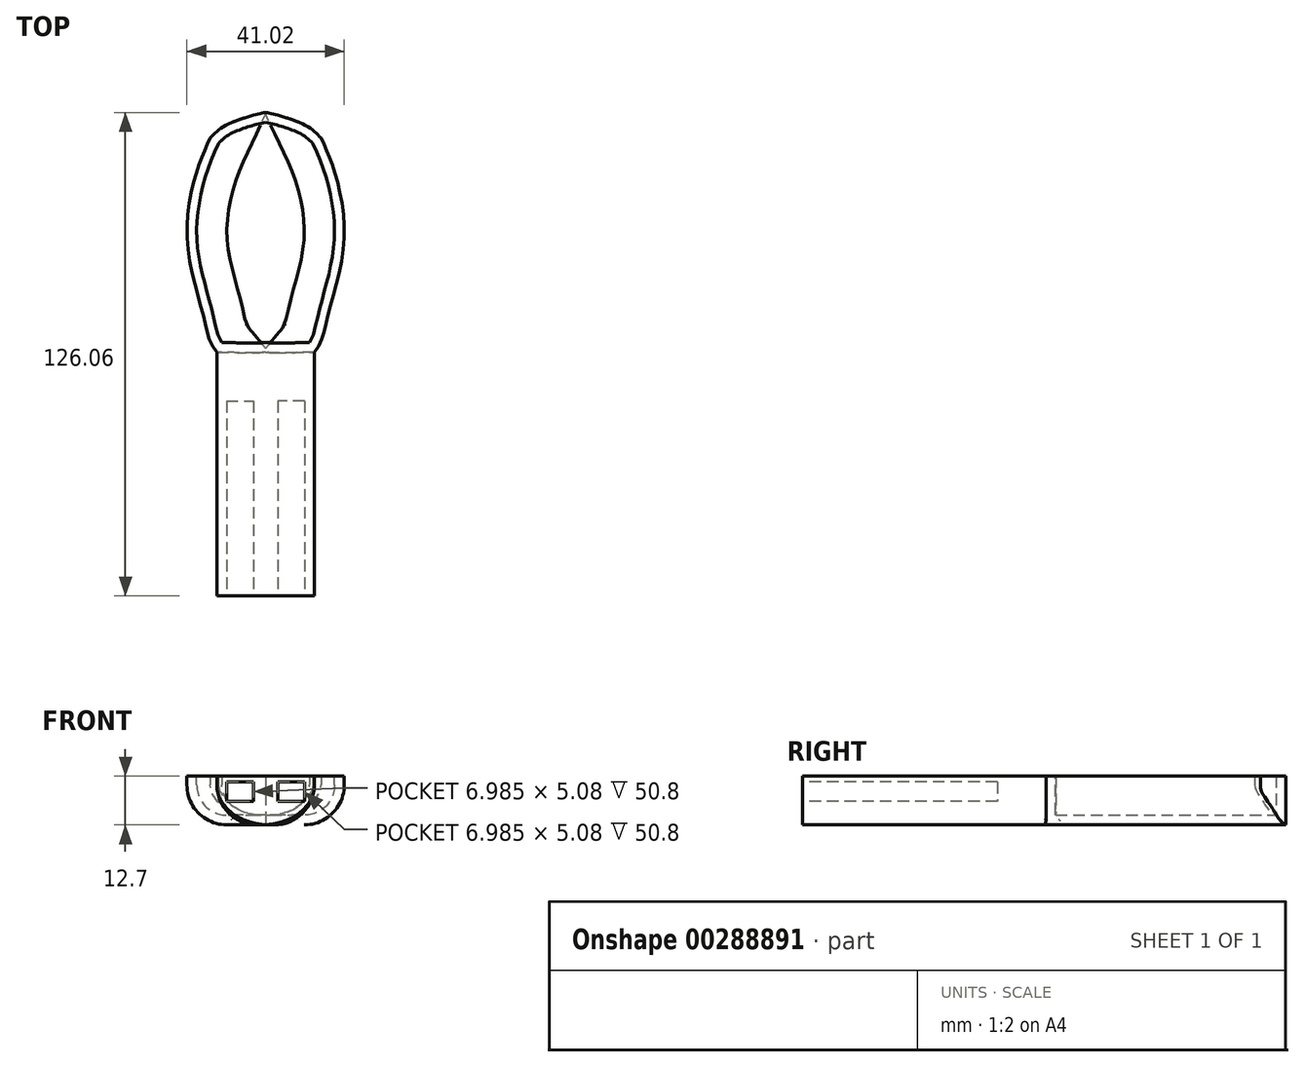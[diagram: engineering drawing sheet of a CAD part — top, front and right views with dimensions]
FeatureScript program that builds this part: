
annotation { "Feature Type Name" : "Feature", "Feature Type Description" : "" }
export const myFeature = defineFeature(function(context is Context, id is Id, definition is map)
    precondition{}
    {
        {
            var Q0;
            Q0=qCreatedBy(makeId("Top.planeOp"),FACE);
            var sketch = newSketch(context, id + "F0", { "sketchPlane" : qUnion([Q0])});
            skLineSegment(sketch, "E0", {"start": v(0, 75.51) * mm, "end": v(0, -68.28) * mm});
            skFitSpline(sketch, "E1", {"points": [v(0, -14.97) * mm, v(-12.7, -14.95) * mm], "startDerivative": vector(-9.63, -0.3) * mm, "endDerivative": vector(-10.55, 0.04) * mm});
            skFitSpline(sketch, "E2", {"points": [v(-12.7, -14.95) * mm, v(-16.24, -5.41) * mm, v(-20.45, 14.44) * mm, v(-17.75, 32.79) * mm, v(-14.44, 40.9) * mm], "startDerivative": vector(-31.58, 37.42) * mm, "endDerivative": vector(17.48, 37.1) * mm});
            skLineSegment(sketch, "E3", {"start": v(-12.7, -14.95) * mm, "end": v(-12.7, -78.45) * mm});
            skLineSegment(sketch, "E4", {"start": v(-12.7, -78.45) * mm, "end": v(0, -78.45) * mm});
            skLineSegment(sketch, "E5", {"start": v(0, -78.45) * mm, "end": v(0, -14.97) * mm});
            skFitSpline(sketch, "E6", {"points": [v(-14.44, 40.9) * mm, v(-10.85, 44) * mm, v(-3.36, 46.84) * mm, v(0, 47.61) * mm], "startDerivative": vector(9.28, 10.13) * mm, "endDerivative": vector(10.75, 2.17) * mm});
            skSolve(sketch);
        }
        {
            var Q0;
            {var subQ0=sQuery(id+"F0.wireOp",EDGE,"E1");Q0=makeQuery(id+"F0.imprint","IMPRINT",FACE,{"disambiguationData":[TD([[makeQuery(id+"F0.imprint","IMPRINT",EDGE,{"derivedFrom":subQ0}),-1.0]])]});}
            extrude(context, id + "F1", {"entities" : qUnion([Q0]), "depth" : 12.7 * mm});
        }
        {
            var Q0;
            Q0=makeQuery(id+"F1.opExtrude","CAP_EDGE",EDGE,{"disambiguationData":[OSD([sQuery(id+"F0.wireOp",EDGE,"E2")])],"isStart":true});
            var Q1;
            Q1=makeQuery(id+"F1.opExtrude","CAP_EDGE",EDGE,{"disambiguationData":[OSD([sQuery(id+"F0.wireOp",EDGE,"6Nhsaj5v-RiRn-NaKJ-OKBq-gLtByNQd9aBa")])],"isStart":true});
            var Q2;
            Q2=makeQuery(id+"F1.opExtrude","CAP_EDGE",EDGE,{"disambiguationData":[OSD([sQuery(id+"F0.wireOp",EDGE,"frloRvQW-Mg0R-VNwh-8u0Y-ItcNmjmq1O22")])],"isStart":true});
            fillet(context, id + "F2", {"entities" : qUnion([Q0, Q1, Q2]), "radius" : 10.4 * mm, "tangentPropagation" : true, "allowEdgeOverflow" : false});
        }
        {
            var Q0;
            Q0=makeQuery(id+"F1.opExtrude","SWEPT_BODY",BODY,{"disambiguationData":[OSD([sQuery(id+"F0.wireOp",EDGE,"E0"),sQuery(id+"F0.wireOp",EDGE,"E1"),sQuery(id+"F0.wireOp",EDGE,"E2"),sQuery(id+"F0.wireOp",EDGE,"6Nhsaj5v-RiRn-NaKJ-OKBq-gLtByNQd9aBa"),sQuery(id+"F0.wireOp",EDGE,"frloRvQW-Mg0R-VNwh-8u0Y-ItcNmjmq1O22")])]});
            var Q1;
            Q1=makeQuery(id+"F1.opExtrude","SWEPT_FACE",FACE,{"disambiguationData":[OSD([sQuery(id+"F0.wireOp",EDGE,"E0")])]});
            mirror(context, id + "F3", {"operationType" : NewBodyOperationType.ADD, "entities" : qUnion([Q0]), "mirrorPlane" : qUnion([Q1])});
        }
        {
            var Q0;
            {var subQ0=makeQuery(id+"F1.opExtrude","CAP_FACE",FACE,{"disambiguationData":[OSD([sQuery(id+"F0.wireOp",EDGE,"E0"),sQuery(id+"F0.wireOp",EDGE,"E1"),sQuery(id+"F0.wireOp",EDGE,"E2"),sQuery(id+"F0.wireOp",EDGE,"6Nhsaj5v-RiRn-NaKJ-OKBq-gLtByNQd9aBa"),sQuery(id+"F0.wireOp",EDGE,"frloRvQW-Mg0R-VNwh-8u0Y-ItcNmjmq1O22")])],"isStart":false});Q0=makeQuery(id+"F3.boolean.opBoolean","MERGE",FACE,{"derivedFrom":[subQ0,makeQuery(id+"F3.opPattern","COPY",FACE,{"derivedFrom":subQ0,"instanceName":"1"})]});}
            var Q1;
            Q1=makeQuery(id+"F1.opExtrude","SWEPT_BODY",BODY,{"disambiguationData":[OSD([sQuery(id+"F0.wireOp",EDGE,"E0"),sQuery(id+"F0.wireOp",EDGE,"E1"),sQuery(id+"F0.wireOp",EDGE,"E2"),sQuery(id+"F0.wireOp",EDGE,"6Nhsaj5v-RiRn-NaKJ-OKBq-gLtByNQd9aBa"),sQuery(id+"F0.wireOp",EDGE,"frloRvQW-Mg0R-VNwh-8u0Y-ItcNmjmq1O22")])]});
            shell(context, id + "F4", {"entities" : qUnion([Q0]), "parts" : qUnion([Q1]), "thickness" : 2.54 * mm});
        }
        {
            var Q0;
            {var subQ0=sQuery(id+"F0.wireOp",EDGE,"E1");Q0=makeQuery(id+"F0.imprint","IMPRINT",FACE,{"disambiguationData":[TD([[makeQuery(id+"F0.imprint","IMPRINT",EDGE,{"derivedFrom":subQ0}),1.0]])]});}
            extrude(context, id + "F5", {"entities" : qUnion([Q0]), "depth" : 12.7 * mm});
        }
        {
            var Q0;
            Q0=makeQuery(id+"F5.opExtrude","CAP_EDGE",EDGE,{"disambiguationData":[OSD([sQuery(id+"F0.wireOp",EDGE,"E3")])],"isStart":true});
            fillet(context, id + "F6", {"entities" : qUnion([Q0]), "radius" : 10.4 * mm, "tangentPropagation" : true, "allowEdgeOverflow" : false});
        }
        {
            var Q0;
            Q0=makeQuery(id+"F5.opExtrude","SWEPT_FACE",FACE,{"disambiguationData":[OSD([sQuery(id+"F0.wireOp",EDGE,"E4")])]});
            var sketch = newSketch(context, id + "F7", { "sketchPlane" : qUnion([Q0])});
            skLineSegment(sketch, "E7", {"start": v(-10.18, 11.18) * mm, "end": v(-10.18, 6.1) * mm});
            skLineSegment(sketch, "E8", {"start": v(-10.18, 11.18) * mm, "end": v(-3.2, 11.18) * mm});
            skLineSegment(sketch, "E9", {"start": v(-3.2, 11.18) * mm, "end": v(-3.2, 6.1) * mm});
            skLineSegment(sketch, "E10", {"start": v(-10.18, 6.1) * mm, "end": v(-3.2, 6.1) * mm});
            skSolve(sketch);
        }
        {
            var Q0;
            Q0=makeQuery(id+"F7.imprint","IMPRINT",FACE,{"disambiguationData":[TD([[makeQuery(id+"F7.imprint","IMPRINT",EDGE,{"derivedFrom":sQuery(id+"F7.wireOp",EDGE,"E7")}),1.0]])]});
            extrude(context, id + "F8", {"entities" : qUnion([Q0]), "operationType" : NewBodyOperationType.REMOVE, "oppositeDirection" : true, "depth" : 50.8 * mm});
        }
        {
            var Q0;
            Q0=makeQuery(id+"F5.opExtrude","SWEPT_BODY",BODY,{"disambiguationData":[OSD([sQuery(id+"F0.wireOp",EDGE,"E1"),sQuery(id+"F0.wireOp",EDGE,"E3"),sQuery(id+"F0.wireOp",EDGE,"E4"),sQuery(id+"F0.wireOp",EDGE,"E5")])]});
            var Q1;
            Q1=qCreatedBy(makeId("Right.planeOp"),FACE);
            mirror(context, id + "F9", {"operationType" : NewBodyOperationType.ADD, "entities" : qUnion([Q0]), "mirrorPlane" : qUnion([Q1])});
        }
    });
